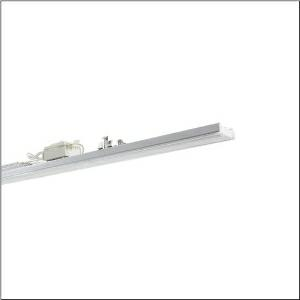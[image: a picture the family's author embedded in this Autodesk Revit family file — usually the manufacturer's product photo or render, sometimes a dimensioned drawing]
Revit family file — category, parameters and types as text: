
# Revit family: licross_r__11_recessed_ho_51tl11mn4exs_0107
name_source: partatom
category: Lighting Fixtures
units: mm (PartAtom-declared; Revit-internal decimal feet)

## family parameters
Cut with Voids When Loaded = No
Host = Face
Light Source = No
Part Type = Normal
Room Calculation Point = No
Round Connector Dimension = Use Diameter
Shared = No

## types (1)
- --- (1 x LED, 14070 lm, 74.5 W, 4000K)
    Apparent Load = 75 VA
    CIE Flux Codes = 87 95 99 100 100
    Color Rendering = 80
    Color Temperature = 4000K
    Default Elevation = 1800 mm
    Description = Licross® 11 Recessed HO, luminaire insert, of sheet steel, coil coated, white, length: 1.500mm, width: 66mm, height: 67mm, LED rated luminous flux: 14.070lm, light colour: 840, control gear: ON/OFF Multilumen, with plug, 3-pole, with phase selection, mains connection: 220..240V, AC, 50/60Hz, rated input power: 75W, halogen-free wiring, primary light control with lens, of plastic, primary optical cover: cover, of PMMA, light emission: direct distribution, primary light characteristic: symmetric, protection rating (complete): IP40, insulation class (complete): insulation class I (protective earthing), certification: CE, ENEC, VDE, UKCA, protection symbol: D if used in an environment without relevant dust loads with corresponding accessories, impact resistance: IK06, permissible ambient temperature for indoor applications: -35..+35°C, corresponds to IFS (International Featured Standards) requirements for safety and quality in the food industry, reducing of maximum allowable ambient temperature of 5°C with ceiling mounting, packaging unit: 1 piece
    Height = 58 mm
    Lamp = 1 x LED
    Lamp Light Flux = 14070 lm
    Lamp Power = 74.5 W
    Lamp count = 1
    Length = 1500 mm
    Luminous efficacy = 189 lm/W
    Manufacturer = Siteco
    ModVariant = No
    Model = 51TL11MN4EXS
    Mounting Place = Ceiling
    Mounting Type = Pendant
    Number of Poles = 1
    OnlyDefault = Yes
    Power Factor = 1
    Product Name = Licross® 11 Recessed HO
    Product group = luminaire insert
    ProductGroupID = 902
    Protection Class = Protection class I
    Protection Degree = IP 40
    RLX_Detail_Level = 1
    RLX_Emergency_Light_Flux = 0 lm
    RLX_Emergency_Type = 0
    RLX_Emergency_Type_DB = No
    RlxData = <blob elided: 22121 chars, md5=abd076e9>
    Socket = socket
    Standby Power = 0 W
    System Light Flux = 14070 lm
    System Power = 75 W
    Type Comments = factory setting: luminous flux: 100 % | (A | C | E) | 174 mA
    Type Image = l_1296930.jpg
    URL = http://relux.com
    VarID = @adj_084582
    Voltage = 0 V
    Weight = 0.00 kg
    Width = 66 mm

## geometry (parser evidence)
native form markers: Blend x4, Sweep x10
no freeform markers — native parametric forms only
